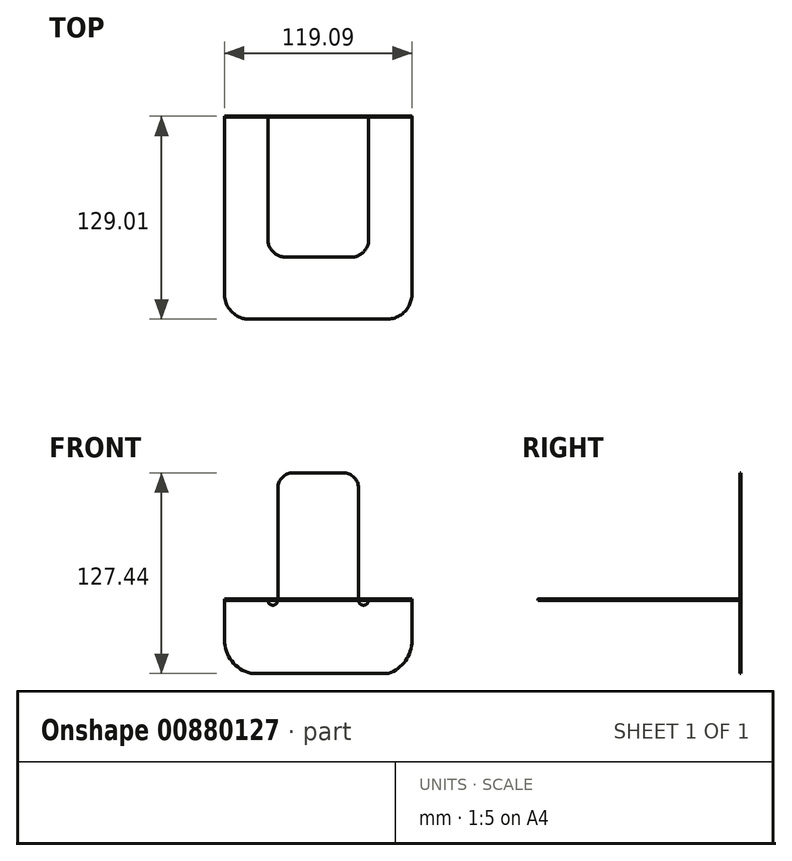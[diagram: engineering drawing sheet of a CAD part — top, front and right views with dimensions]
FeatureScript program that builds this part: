
annotation { "Feature Type Name" : "Feature", "Feature Type Description" : "" }
export const myFeature = defineFeature(function(context is Context, id is Id, definition is map)
    precondition{}
    {
        {
            var Q0;
            Q0=qCreatedBy(makeId("Front.planeOp"),FACE);
            var sketch = newSketch(context, id + "F0", { "sketchPlane" : qUnion([Q0])});
            skLineSegment(sketch, "E0.left", {"start": v(-59.54, -6.75) * mm, "end": v(-59.54, -31.81) * mm});
            skLineSegment(sketch, "E0.right", {"start": v(59.53, -6.75) * mm, "end": v(59.53, -32.35) * mm});
            skArc(sketch, "E1", {"start": v(-59.54, -31.81) * mm, "mid": v(-54.82, -45.42) * mm, "end": v(-42.7, -53.2) * mm});
            skArc(sketch, "E2", {"start": v(59.53, -32.35) * mm, "mid": v(55.4, -45.18) * mm, "end": v(44.58, -53.2) * mm});
            skLineSegment(sketch, "E3", {"start": v(-42.7, -53.2) * mm, "end": v(44.58, -53.2) * mm});
            skLineSegment(sketch, "E4", {"start": v(-25.64, -6.75) * mm, "end": v(-25.64, 64.4) * mm});
            skLineSegment(sketch, "E5", {"start": v(25.64, -6.75) * mm, "end": v(25.64, 64.4) * mm});
            skLineSegment(sketch, "E6", {"start": v(15.8, 74.24) * mm, "end": v(-15.8, 74.24) * mm});
            skArc(sketch, "E7", {"start": v(-15.8, 74.24) * mm, "mid": v(-22.76, 71.36) * mm, "end": v(-25.64, 64.4) * mm});
            skArc(sketch, "E8.MirrorCS", {"start": v(15.8, 74.24) * mm, "mid": v(22.76, 71.36) * mm, "end": v(25.64, 64.4) * mm});
            skPoint(sketch, "E9.orphan", {"position": v(25.64, 74.24) * mm});
            skPoint(sketch, "E10.orphan", {"position": v(-25.64, 74.24) * mm});
            skLineSegment(sketch, "E11", {"start": v(-59.54, -6.75) * mm, "end": v(-31.98, -6.75) * mm});
            skLineSegment(sketch, "E12.MirrorCS", {"start": v(59.54, -6.75) * mm, "end": v(31.98, -6.75) * mm});
            skArc(sketch, "E13", {"start": v(-25.64, -6.75) * mm, "mid": v(-28.81, -9.91) * mm, "end": v(-31.98, -6.75) * mm});
            skArc(sketch, "E14", {"start": v(25.64, -6.75) * mm, "mid": v(28.81, -9.91) * mm, "end": v(31.98, -6.75) * mm});
            skSolve(sketch);
        }
        {
            var Q0;
            Q0 = qSketchRegion(id + "F0", true);
            extrude(context, id + "F1", {"entities" : qUnion([Q0]), "depth" : 0.62 * mm, "offsetDistance" : 25 * mm});
        }
        {
            var Q0;
            Q0=makeQuery(id+"F1.opExtrude","SWEPT_FACE",FACE,{"disambiguationData":[OSD([sQuery(id+"F0.wireOp",EDGE,"E0.left")])]});
            var sketch = newSketch(context, id + "F2", { "sketchPlane" : qUnion([Q0])});
            skLineSegment(sketch, "E15", {"start": v(0, -6.75) * mm, "end": v(128.39, -6.75) * mm});
            skLineSegment(sketch, "E16", {"start": v(128.39, -6.75) * mm, "end": v(128.39, -5.92) * mm});
            skArc(sketch, "E17", {"start": v(0.62, -5.92) * mm, "mid": v(0.17, -6.23) * mm, "end": v(0, -6.75) * mm});
            skLineSegment(sketch, "E18", {"start": v(0.62, -5.92) * mm, "end": v(128.39, -5.92) * mm});
            skSolve(sketch);
        }
        {
            var Q0;
            Q0 = qSketchRegion(id + "F2", true);
            extrude(context, id + "F3", {"entities" : qUnion([Q0]), "operationType" : NewBodyOperationType.ADD, "oppositeDirection" : true, "depth" : 27.54 * mm, "offsetDistance" : 25 * mm});
        }
        {
            var Q0;
            Q0=makeQuery(id+"F1.opExtrude","SWEPT_FACE",FACE,{"disambiguationData":[OSD([sQuery(id+"F0.wireOp",EDGE,"E0.right")])]});
            var sketch = newSketch(context, id + "F4", { "sketchPlane" : qUnion([Q0])});
            skArc(sketch, "E19", {"start": v(0, -6.75) * mm, "mid": v(-0.17, -6.24) * mm, "end": v(-0.62, -5.93) * mm});
            skLineSegment(sketch, "E20", {"start": v(0, -6.75) * mm, "end": v(-129, -6.75) * mm});
            skLineSegment(sketch, "E21", {"start": v(-129, -6.75) * mm, "end": v(-129, -5.92) * mm});
            skLineSegment(sketch, "E22", {"start": v(-129, -5.92) * mm, "end": v(-0.62, -5.93) * mm});
            skSolve(sketch);
        }
        {
            var Q0;
            Q0 = qSketchRegion(id + "F4", true);
            extrude(context, id + "F5", {"entities" : qUnion([Q0]), "operationType" : NewBodyOperationType.ADD, "oppositeDirection" : true, "depth" : 27.55 * mm, "offsetDistance" : 25 * mm});
        }
        {
            var Q0;
            Q0=makeQuery(id+"F5.opExtrude","SWEPT_FACE",FACE,{"disambiguationData":[OSD([sQuery(id+"F4.wireOp",EDGE,"E20")])]});
            var sketch = newSketch(context, id + "F6", { "sketchPlane" : qUnion([Q0])});
            skLineSegment(sketch, "E23", {"start": v(59.53, 129) * mm, "end": v(-59.55, 129) * mm});
            skLineSegment(sketch, "E24", {"start": v(-59.55, 129) * mm, "end": v(-59.55, 128.32) * mm});
            skLineSegment(sketch, "E25", {"start": v(31.98, 89.58) * mm, "end": v(-32, 89.58) * mm});
            skArc(sketch, "E26", {"start": v(31.98, 75.55) * mm, "mid": v(28.73, 86.33) * mm, "end": v(17.95, 89.58) * mm});
            skArc(sketch, "E27", {"start": v(-20.17, 89.58) * mm, "mid": v(-29.36, 85.32) * mm, "end": v(-32.01, 75.55) * mm});
            skLineSegment(sketch, "E28", {"start": v(-59.55, 128.32) * mm, "end": v(-59.55, 75.55) * mm});
            skLineSegment(sketch, "E29", {"start": v(-59.55, 75.55) * mm, "end": v(-32.01, 75.55) * mm});
            skLineSegment(sketch, "E30", {"start": v(59.53, 129) * mm, "end": v(59.53, 75.55) * mm});
            skLineSegment(sketch, "E31", {"start": v(59.53, 75.55) * mm, "end": v(31.98, 75.55) * mm});
            skSolve(sketch);
        }
        {
            var Q0;
            Q0 = qSketchRegion(id + "F6", true);
            var Q1;
            Q1=makeQuery(id+"F5.opExtrude","SWEPT_FACE",FACE,{"disambiguationData":[OSD([sQuery(id+"F4.wireOp",EDGE,"E22")])]});
            extrude(context, id + "F7", {"entities" : qUnion([Q0]), "operationType" : NewBodyOperationType.ADD, "endBound" : BoundingType.UP_TO_SURFACE, "oppositeDirection" : true, "depth" : 25 * mm, "endBoundEntityFace" : qUnion([Q1]), "offsetDistance" : 25 * mm});
        }
        {
            var Q0;
            Q0=makeQuery(id+"F7.boolean.opBoolean","MERGE",FACE,{"derivedFrom":[makeQuery(id+"F3.opExtrude","SWEPT_FACE",FACE,{"disambiguationData":[OSD([sQuery(id+"F2.wireOp",EDGE,"E15")])]}),makeQuery(id+"F5.opExtrude","SWEPT_FACE",FACE,{"disambiguationData":[OSD([sQuery(id+"F4.wireOp",EDGE,"E20")])]}),makeQuery(id+"F7.opExtrude","CAP_FACE",FACE,{"disambiguationData":[OSD([sQuery(id+"F6.wireOp",EDGE,"E23"),sQuery(id+"F6.wireOp",EDGE,"E24"),sQuery(id+"F6.wireOp",EDGE,"E25"),sQuery(id+"F6.wireOp",EDGE,"E26"),sQuery(id+"F6.wireOp",EDGE,"E27"),sQuery(id+"F6.wireOp",EDGE,"E28"),sQuery(id+"F6.wireOp",EDGE,"E29"),sQuery(id+"F6.wireOp",EDGE,"E30"),sQuery(id+"F6.wireOp",EDGE,"E31")])],"isStart":true})]});
            var sketch = newSketch(context, id + "F8", { "sketchPlane" : qUnion([Q0])});
            skArc(sketch, "E32", {"start": v(-43.55, 129) * mm, "mid": v(-54.86, 124.32) * mm, "end": v(-59.55, 113) * mm});
            skArc(sketch, "E33.MirrorCS", {"start": v(43.55, 129) * mm, "mid": v(54.86, 124.32) * mm, "end": v(59.55, 113) * mm});
            skLineSegment(sketch, "E34", {"start": v(-59.55, 113) * mm, "end": v(-59.55, 129) * mm});
            skLineSegment(sketch, "E35", {"start": v(-59.55, 129) * mm, "end": v(-43.55, 129) * mm});
            skLineSegment(sketch, "E36", {"start": v(43.55, 129) * mm, "end": v(59.53, 129) * mm});
            skLineSegment(sketch, "E37", {"start": v(59.53, 129) * mm, "end": v(59.55, 113) * mm});
            skSolve(sketch);
        }
        {
            var Q0;
            Q0 = qSketchRegion(id + "F8", true);
            extrude(context, id + "F9", {"entities" : qUnion([Q0]), "operationType" : NewBodyOperationType.REMOVE, "oppositeDirection" : true, "depth" : 25 * mm, "offsetDistance" : 25 * mm});
        }
    });
